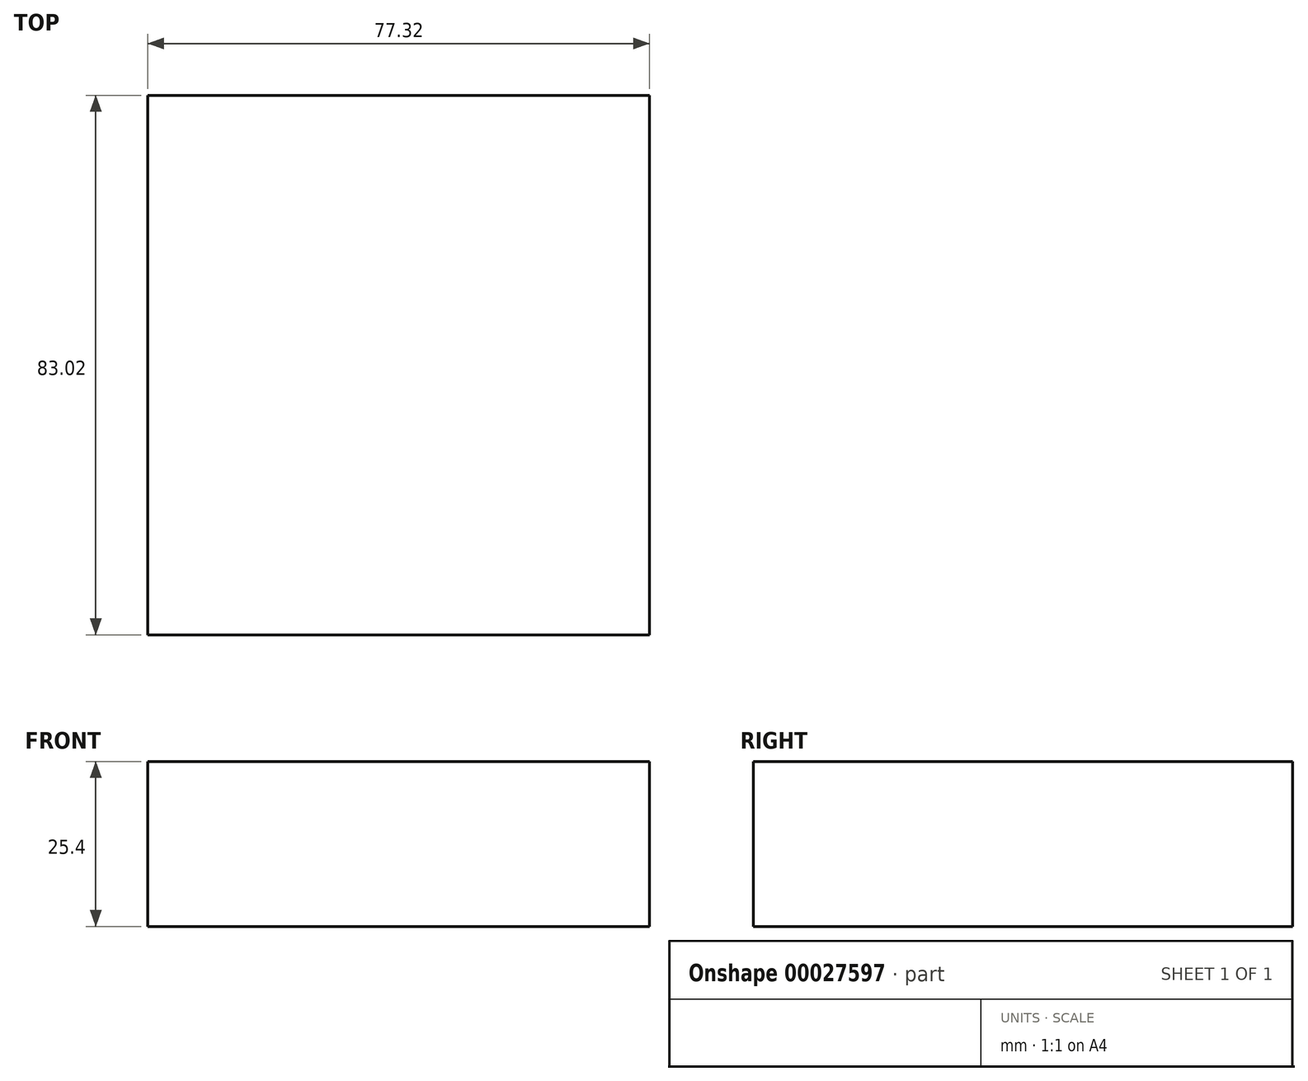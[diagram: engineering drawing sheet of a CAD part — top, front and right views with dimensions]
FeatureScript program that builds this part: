
annotation { "Feature Type Name" : "Feature", "Feature Type Description" : "" }
export const myFeature = defineFeature(function(context is Context, id is Id, definition is map)
    precondition{}
    {
        {
            var Q0;
            Q0=qCreatedBy(makeId("Top.planeOp"),FACE);
            var sketch = newSketch(context, id + "F0", { "sketchPlane" : qUnion([Q0])});
            skLineSegment(sketch, "E0.rect.bottom", {"start": v(38.66, 41.51) * mm, "end": v(-38.66, 41.51) * mm});
            skLineSegment(sketch, "E0.rect.top", {"start": v(38.66, -41.51) * mm, "end": v(-38.66, -41.51) * mm});
            skLineSegment(sketch, "E0.rect.left", {"start": v(38.66, 41.51) * mm, "end": v(38.66, -41.51) * mm});
            skLineSegment(sketch, "E0.rect.right", {"start": v(-38.66, 41.51) * mm, "end": v(-38.66, -41.51) * mm});
            skPoint(sketch, "E0.rect.middle", {"position": v(0, 0) * mm});
            skSolve(sketch);
        }
        {
            var Q0;
            Q0=makeQuery(id+"F0.imprint","IMPRINT",FACE,{"disambiguationData":[TD([[makeQuery(id+"F0.imprint","IMPRINT",EDGE,{"derivedFrom":sQuery(id+"F0.wireOp",EDGE,"E0.rect.bottom")}),1.0]])]});
            extrude(context, id + "F1", {"entities" : qUnion([Q0]), "depth" : 25.4 * mm});
        }
    });
